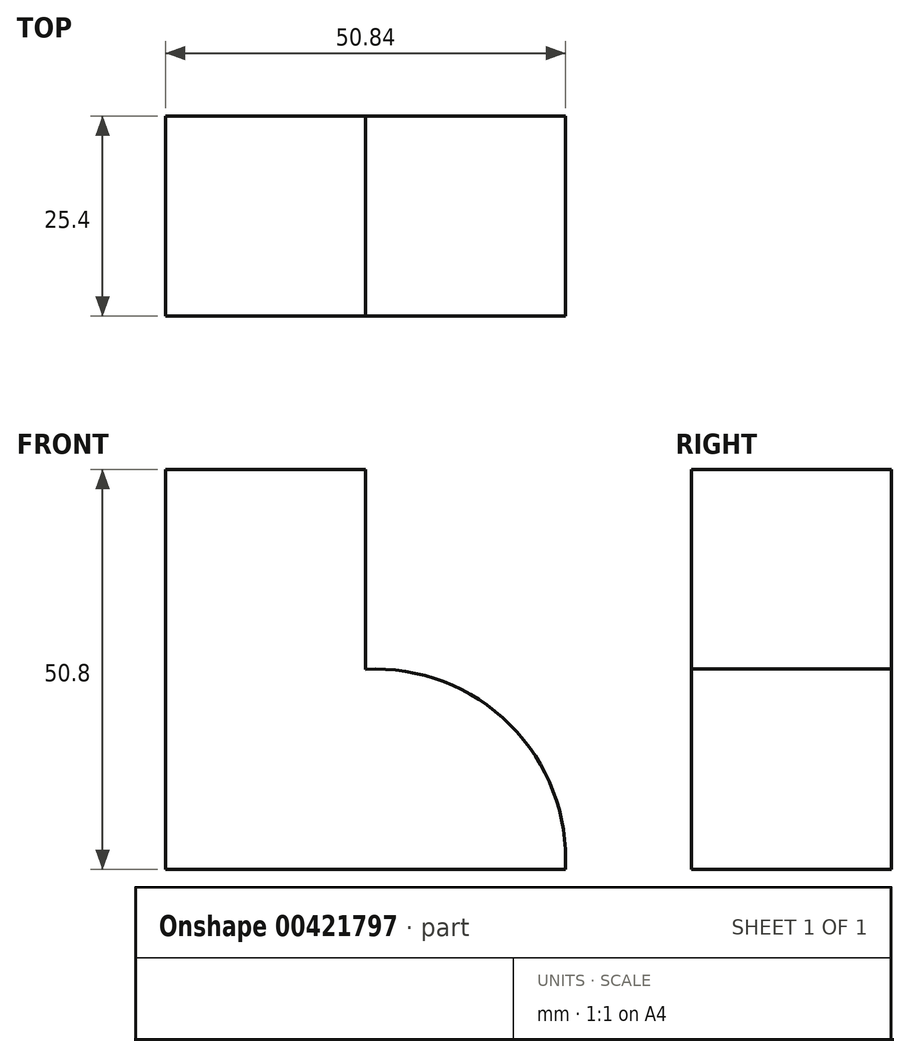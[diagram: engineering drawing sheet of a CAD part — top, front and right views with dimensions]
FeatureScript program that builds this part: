
annotation { "Feature Type Name" : "Feature", "Feature Type Description" : "" }
export const myFeature = defineFeature(function(context is Context, id is Id, definition is map)
    precondition{}
    {
        {
            var Q0;
            Q0=qCreatedBy(makeId("Front.planeOp"),FACE);
            var sketch = newSketch(context, id + "F0", { "sketchPlane" : qUnion([Q0])});
            skLineSegment(sketch, "E0", {"start": v(0, 0) * mm, "end": v(0, 50.8) * mm});
            skLineSegment(sketch, "E1", {"start": v(0, 50.8) * mm, "end": v(0, 0) * mm});
            skLineSegment(sketch, "E2", {"start": v(0, 0) * mm, "end": v(50.8, 0) * mm});
            skLineSegment(sketch, "E3", {"start": v(0, 50.8) * mm, "end": v(25.4, 50.8) * mm});
            skLineSegment(sketch, "E4", {"start": v(25.4, 50.8) * mm, "end": v(25.4, 25.4) * mm});
            skArc(sketch, "E5", {"start": v(50.8, 0) * mm, "mid": v(43.78, 18.38) * mm, "end": v(25.4, 25.4) * mm});
            skSolve(sketch);
        }
        {
            var Q0;
            Q0 = qSketchRegion(id + "F0", true);
            extrude(context, id + "F1", {"entities" : qUnion([Q0]), "depth" : 25.4 * mm});
        }
    });
